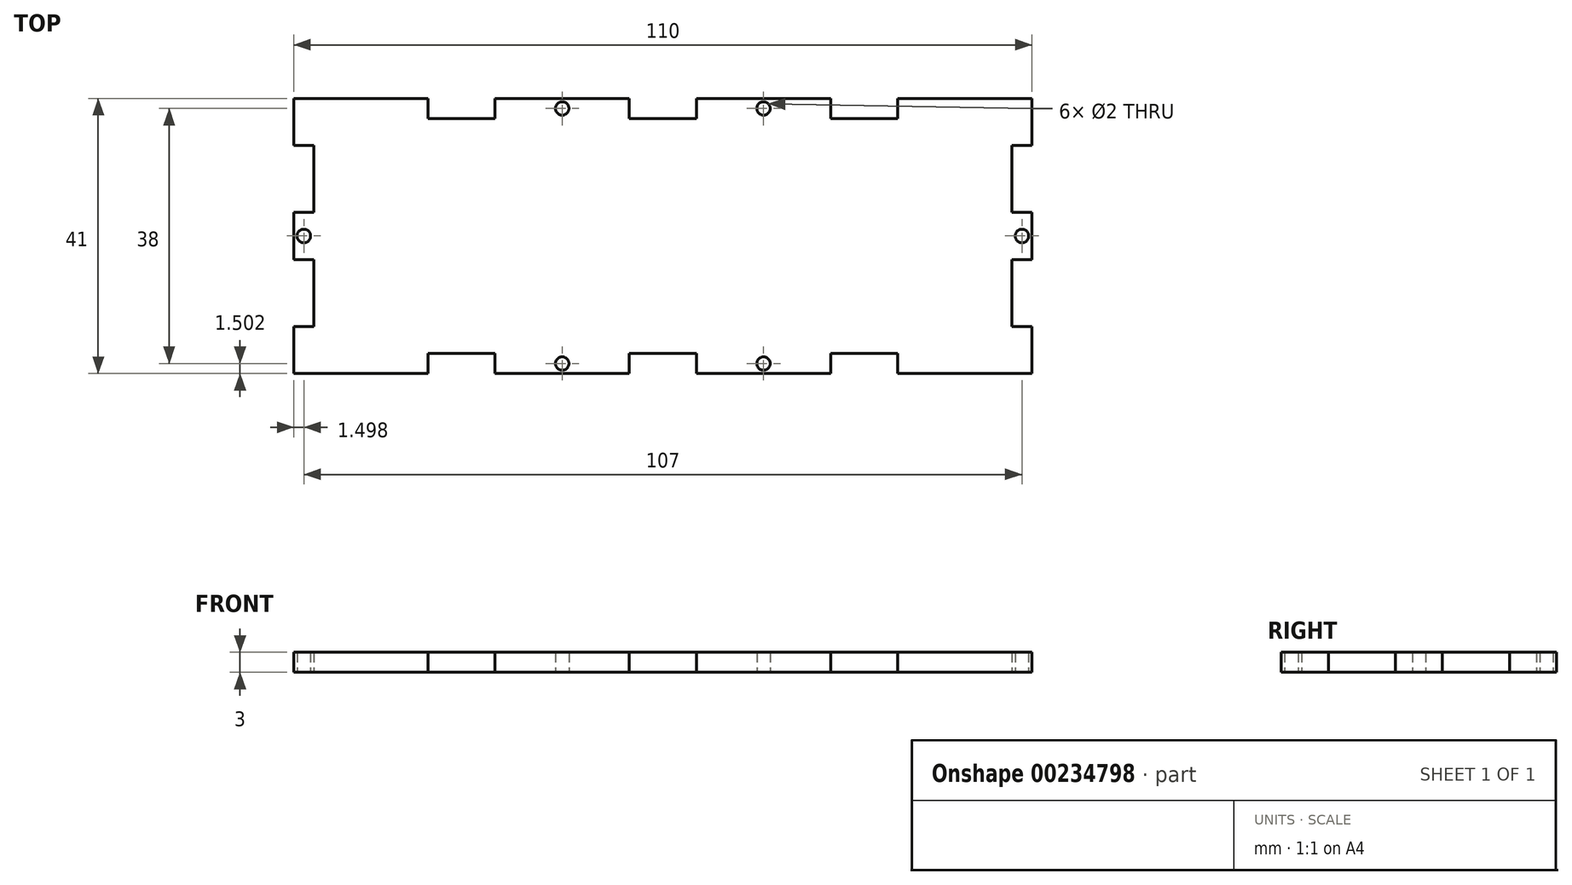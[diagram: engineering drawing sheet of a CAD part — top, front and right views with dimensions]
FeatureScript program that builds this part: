
annotation { "Feature Type Name" : "Feature", "Feature Type Description" : "" }
export const myFeature = defineFeature(function(context is Context, id is Id, definition is map)
    precondition{}
    {
        {
            var Q0;
            Q0=qCreatedBy(makeId("Top.planeOp"),FACE);
            var sketch = newSketch(context, id + "F0", { "sketchPlane" : qUnion([Q0])});
            skLineSegment(sketch, "E0.bottom", {"start": v(-8.84, -0.43) * mm, "end": v(11.16, -0.43) * mm});
            skLineSegment(sketch, "E0.top", {"start": v(-8.84, -41.43) * mm, "end": v(11.16, -41.43) * mm});
            skLineSegment(sketch, "E0.left", {"start": v(-8.84, -0.43) * mm, "end": v(-8.84, -7.43) * mm});
            skLineSegment(sketch, "E0.right", {"start": v(101.16, -0.43) * mm, "end": v(101.16, -7.43) * mm});
            skPoint(sketch, "E1", {"position": v(11.16, -0.43) * mm});
            skPoint(sketch, "E2", {"position": v(81.16, -0.43) * mm});
            skPoint(sketch, "E3", {"position": v(71.16, -0.43) * mm});
            skPoint(sketch, "E4", {"position": v(51.16, -0.43) * mm});
            skLineSegment(sketch, "E5", {"start": v(11.16, -0.43) * mm, "end": v(11.16, -3.43) * mm});
            skLineSegment(sketch, "E6", {"start": v(11.16, -3.43) * mm, "end": v(21.16, -3.43) * mm});
            skLineSegment(sketch, "E7", {"start": v(21.16, -3.43) * mm, "end": v(21.16, -0.43) * mm});
            skLineSegment(sketch, "E8", {"start": v(41.16, -0.43) * mm, "end": v(41.16, -3.43) * mm});
            skLineSegment(sketch, "E9", {"start": v(41.16, -3.43) * mm, "end": v(51.16, -3.43) * mm});
            skLineSegment(sketch, "E10", {"start": v(51.16, -3.43) * mm, "end": v(51.16, -0.43) * mm});
            skLineSegment(sketch, "E11", {"start": v(71.16, -0.43) * mm, "end": v(71.16, -3.43) * mm});
            skLineSegment(sketch, "E12", {"start": v(71.16, -3.43) * mm, "end": v(81.16, -3.43) * mm});
            skLineSegment(sketch, "E13", {"start": v(81.16, -3.43) * mm, "end": v(81.16, -0.43) * mm});
            skLineSegment(sketch, "E14.trimOffspring", {"start": v(21.16, -0.43) * mm, "end": v(41.16, -0.43) * mm});
            skLineSegment(sketch, "E15.trimOffspring", {"start": v(51.16, -0.43) * mm, "end": v(71.16, -0.43) * mm});
            skLineSegment(sketch, "E16.trimOffspring", {"start": v(81.16, -0.43) * mm, "end": v(101.16, -0.43) * mm});
            skLineSegment(sketch, "E17.MirrorCS", {"start": v(81.16, -38.43) * mm, "end": v(81.16, -41.43) * mm});
            skLineSegment(sketch, "E18.MirrorCS", {"start": v(41.16, -41.43) * mm, "end": v(41.16, -38.43) * mm});
            skLineSegment(sketch, "E19.MirrorCS", {"start": v(21.16, -38.43) * mm, "end": v(21.16, -41.43) * mm});
            skLineSegment(sketch, "E20.MirrorCS", {"start": v(71.16, -41.43) * mm, "end": v(71.16, -38.43) * mm});
            skLineSegment(sketch, "E21.MirrorCS", {"start": v(11.16, -41.43) * mm, "end": v(11.16, -38.43) * mm});
            skLineSegment(sketch, "E22.MirrorCS", {"start": v(51.16, -38.43) * mm, "end": v(51.16, -41.43) * mm});
            skPoint(sketch, "E23.MirrorP", {"position": v(51.16, -41.43) * mm});
            skLineSegment(sketch, "E24.MirrorCS", {"start": v(71.16, -38.43) * mm, "end": v(81.16, -38.43) * mm});
            skLineSegment(sketch, "E25.MirrorCS", {"start": v(41.16, -38.43) * mm, "end": v(51.16, -38.43) * mm});
            skPoint(sketch, "E26.MirrorP", {"position": v(81.16, -41.43) * mm});
            skPoint(sketch, "E27.MirrorP", {"position": v(71.16, -41.43) * mm});
            skLineSegment(sketch, "E28.MirrorCS", {"start": v(11.16, -38.43) * mm, "end": v(21.16, -38.43) * mm});
            skLineSegment(sketch, "E29.MirrorCS", {"start": v(51.16, -41.43) * mm, "end": v(71.16, -41.43) * mm});
            skLineSegment(sketch, "E30.MirrorCS", {"start": v(21.16, -41.43) * mm, "end": v(41.16, -41.43) * mm});
            skPoint(sketch, "E31.MirrorP", {"position": v(41.16, -41.43) * mm});
            skPoint(sketch, "E32.MirrorP", {"position": v(11.16, -41.43) * mm});
            skLineSegment(sketch, "E33.MirrorCS", {"start": v(81.16, -41.43) * mm, "end": v(101.16, -41.43) * mm});
            skPoint(sketch, "E34.MirrorP", {"position": v(21.16, -41.43) * mm});
            skPoint(sketch, "E35", {"position": v(-8.84, -7.43) * mm});
            skPoint(sketch, "E36", {"position": v(-8.84, -34.43) * mm});
            skPoint(sketch, "E37", {"position": v(-8.84, -17.43) * mm});
            skPoint(sketch, "E38", {"position": v(-8.84, -24.43) * mm});
            skPoint(sketch, "E39", {"position": v(-8.84, -20.93) * mm});
            skLineSegment(sketch, "E40", {"start": v(-8.84, -7.43) * mm, "end": v(-5.84, -7.43) * mm});
            skLineSegment(sketch, "E41", {"start": v(-5.84, -7.43) * mm, "end": v(-5.84, -17.43) * mm});
            skLineSegment(sketch, "E42", {"start": v(-5.84, -17.43) * mm, "end": v(-8.84, -17.43) * mm});
            skLineSegment(sketch, "E43", {"start": v(-8.84, -24.43) * mm, "end": v(-5.84, -24.43) * mm});
            skLineSegment(sketch, "E44", {"start": v(-5.84, -24.43) * mm, "end": v(-5.84, -34.43) * mm});
            skLineSegment(sketch, "E45", {"start": v(-5.84, -34.43) * mm, "end": v(-8.84, -34.43) * mm});
            skLineSegment(sketch, "E46.trimOffspring", {"start": v(-8.84, -17.43) * mm, "end": v(-8.84, -24.43) * mm});
            skLineSegment(sketch, "E47.trimOffspring", {"start": v(-8.84, -34.43) * mm, "end": v(-8.84, -41.43) * mm});
            skLineSegment(sketch, "E48.MirrorCS", {"start": v(98.16, -34.43) * mm, "end": v(101.16, -34.43) * mm});
            skLineSegment(sketch, "E49.MirrorCS", {"start": v(98.16, -17.43) * mm, "end": v(101.16, -17.43) * mm});
            skLineSegment(sketch, "E50.MirrorCS", {"start": v(101.16, -7.43) * mm, "end": v(98.16, -7.43) * mm});
            skLineSegment(sketch, "E51.MirrorCS", {"start": v(101.16, -24.43) * mm, "end": v(98.16, -24.43) * mm});
            skLineSegment(sketch, "E52.MirrorCS", {"start": v(101.16, -17.43) * mm, "end": v(101.16, -24.43) * mm});
            skLineSegment(sketch, "E53.MirrorCS", {"start": v(98.16, -7.43) * mm, "end": v(98.16, -17.43) * mm});
            skPoint(sketch, "E54.MirrorP", {"position": v(101.16, -24.43) * mm});
            skPoint(sketch, "E55.MirrorP", {"position": v(101.16, -17.43) * mm});
            skLineSegment(sketch, "E56.MirrorCS", {"start": v(98.16, -24.43) * mm, "end": v(98.16, -34.43) * mm});
            skLineSegment(sketch, "E57.MirrorCS", {"start": v(101.16, -34.43) * mm, "end": v(101.16, -41.43) * mm});
            skPoint(sketch, "E58.MirrorP", {"position": v(101.16, -34.43) * mm});
            skPoint(sketch, "E59.MirrorP", {"position": v(101.16, -20.93) * mm});
            skPoint(sketch, "E60.MirrorP", {"position": v(101.16, -7.43) * mm});
            skCircle(sketch, "E61", {"center": v(31.16, -1.93) * mm, "radius": 1 * mm});
            skPoint(sketch, "E62", {"position": v(31.16, -0.43) * mm});
            skPoint(sketch, "E63", {"position": v(21.16, -1.93) * mm});
            skPoint(sketch, "E64", {"position": v(51.16, -1.93) * mm});
            skPoint(sketch, "E65", {"position": v(61.16, -0.43) * mm});
            skCircle(sketch, "E66", {"center": v(61.16, -1.93) * mm, "radius": 1 * mm});
            skPoint(sketch, "E67", {"position": v(-7.34, -17.43) * mm});
            skCircle(sketch, "E68", {"center": v(-7.34, -20.93) * mm, "radius": 1 * mm});
            skCircle(sketch, "E69.MirrorC", {"center": v(31.16, -39.93) * mm, "radius": 1 * mm});
            skCircle(sketch, "E70.MirrorC", {"center": v(61.16, -39.93) * mm, "radius": 1 * mm});
            skCircle(sketch, "E71.MirrorC", {"center": v(99.66, -20.93) * mm, "radius": 1 * mm});
            skSolve(sketch);
        }
        {
            var Q0;
            Q0=makeQuery(id+"F0.imprint","IMPRINT",FACE,{"disambiguationData":[TD([[makeQuery(id+"F0.imprint","IMPRINT",EDGE,{"derivedFrom":sQuery(id+"F0.wireOp",EDGE,"E0.bottom")}),-1.0]])]});
            extrude(context, id + "F1", {"entities" : qUnion([Q0]), "endBound" : BoundingType.SYMMETRIC, "depth" : 3 * mm});
        }
    });
